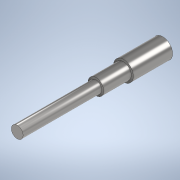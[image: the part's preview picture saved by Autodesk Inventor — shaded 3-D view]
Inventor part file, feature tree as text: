
AUTODESK INVENTOR PART (.ipt)
format: ipt  version: 2021 (Build 250183000, 183)  size: 113,664 bytes
history: native  units: in
note: dims shown in document units (in); Inventor stores cm internally (conversion verified against a paired STEP export)
features: extrude x3, sketch x3
ambient origin geometry x8: Origin, YZ Plane, XZ Plane, XY Plane, X Axis, Y Axis, Z Axis, Center Point
bodies: Solid1 (feature_tree)
feature tree (6):
  extrude  "Extrusion1"  Depth=39.3701in TaperAngle=0.0deg
  extrude  "Extrusion2"  Depth=27.5591in TaperAngle=0.0deg
  extrude  "Extrusion3"  Depth=78.7402in TaperAngle=0.0deg
  sketch  "Sketch1"  dims[d0=19.685in d1=39.3701in d2=0.0in]
  sketch  "Sketch2"  dims[d3=15.748in d4=27.5591in d5=0.0in]
  sketch  "Sketch3"  dims[d6=11.811in d7=78.7402in d8=0.0in]
